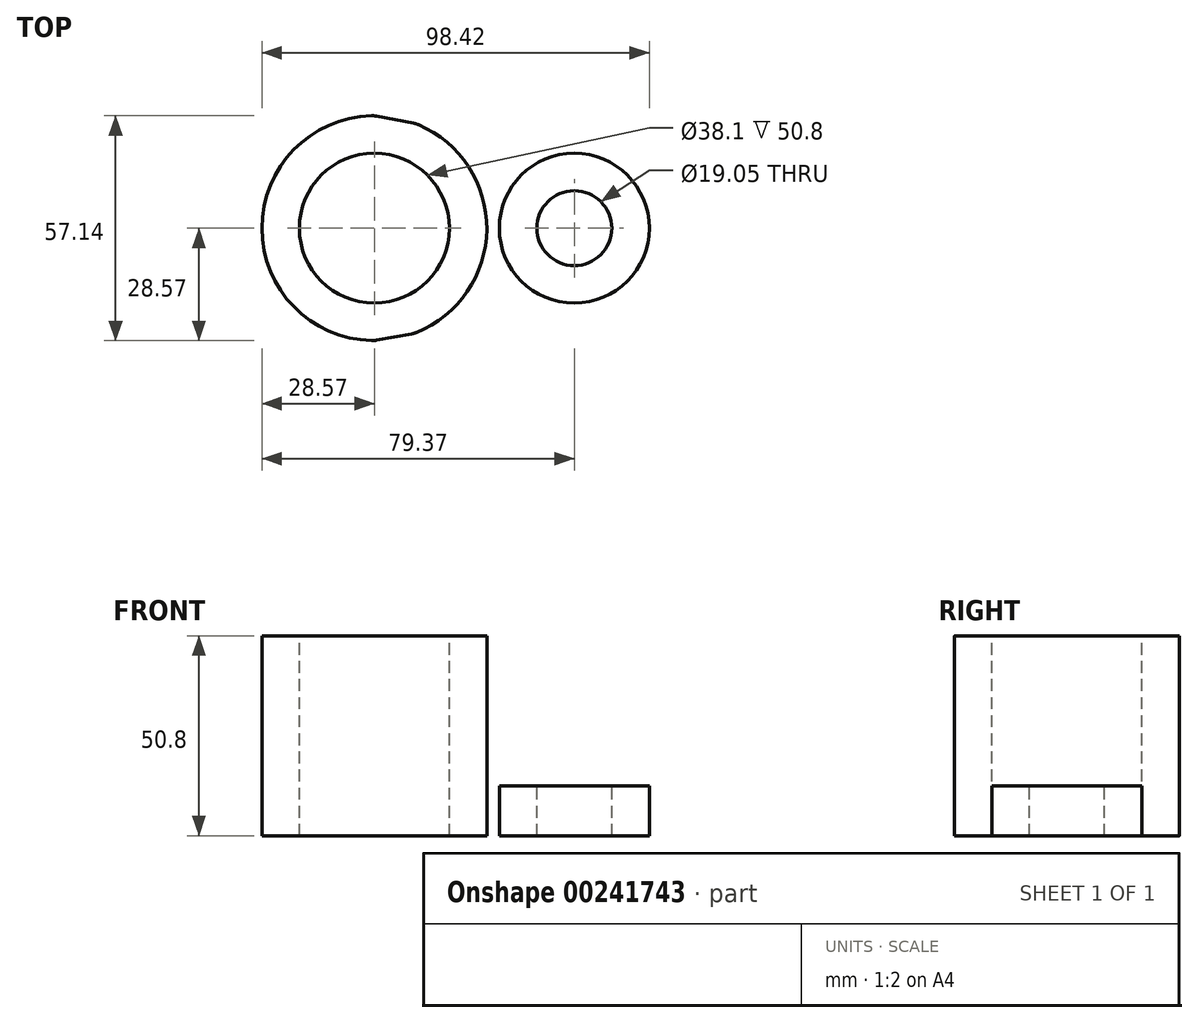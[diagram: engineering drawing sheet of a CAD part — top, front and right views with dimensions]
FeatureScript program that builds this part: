
annotation { "Feature Type Name" : "Feature", "Feature Type Description" : "" }
export const myFeature = defineFeature(function(context is Context, id is Id, definition is map)
    precondition{}
    {
        {
            var Q0;
            Q0=qCreatedBy(makeId("Top.planeOp"),FACE);
            var sketch = newSketch(context, id + "F0", { "sketchPlane" : qUnion([Q0])});
            skCircle(sketch, "E0", {"center": v(0, 0) * mm, "radius": 28.58 * mm});
            skCircle(sketch, "E1", {"center": v(0, 0) * mm, "radius": 19.05 * mm});
            skCircle(sketch, "E2", {"center": v(50.8, 0) * mm, "radius": 9.53 * mm});
            skCircle(sketch, "E3", {"center": v(50.8, 0) * mm, "radius": 19.05 * mm});
            skLineSegment(sketch, "E4", {"start": v(0, 28.57) * mm, "end": v(49.87, 19.03) * mm});
            skLineSegment(sketch, "E5", {"start": v(0, -28.58) * mm, "end": v(54.2, -18.74) * mm});
            skSolve(sketch);
        }
        {
            var Q0;
            Q0=makeQuery(id+"F0.imprint","IMPRINT",FACE,{"disambiguationData":[TD([[makeQuery(id+"F0.imprint","IMPRINT",EDGE,{"derivedFrom":sQuery(id+"F0.wireOp",EDGE,"E2")}),-1.0]])]});
            var Q1;
            {var subQ0=sQuery(id+"F0.wireOp",EDGE,"E4");var subQ1=sQuery(id+"F0.wireOp",EDGE,"E0");var subQ2=makeQuery(id+"F0.imprint","INTERSECT",VERTEX,{"disambiguationData":[OD(1.0)],"derivedFrom":[subQ1,subQ0]});Q1=makeQuery(id+"F0.imprint","IMPRINT",FACE,{"disambiguationData":[TD([[makeQuery(id+"F0.imprint","IMPRINT",EDGE,{"disambiguationData":[TD([[subQ2,1.0]])],"derivedFrom":subQ1}),-1.0]])]});}
            var Q2;
            Q2=makeQuery(id+"F0.imprint","IMPRINT",FACE,{"disambiguationData":[TD([[makeQuery(id+"F0.imprint","IMPRINT",EDGE,{"derivedFrom":sQuery(id+"F0.wireOp",EDGE,"E1")}),-1.0]])]});
            extrude(context, id + "F1", {"entities" : qUnion([Q0, Q1, Q2]), "oppositeDirection" : true, "depth" : 25.4 * mm});
        }
        {
            var Q0;
            Q0=makeQuery(id+"F0.imprint","IMPRINT",FACE,{"disambiguationData":[TD([[makeQuery(id+"F0.imprint","IMPRINT",EDGE,{"derivedFrom":sQuery(id+"F0.wireOp",EDGE,"E1")}),-1.0]])]});
            var Q1;
            {var subQ0=sQuery(id+"F0.wireOp",EDGE,"E5");var subQ1=sQuery(id+"F0.wireOp",EDGE,"E0");var subQ2=makeQuery(id+"F0.imprint","INTERSECT",VERTEX,{"disambiguationData":[OD(0.0)],"derivedFrom":[subQ1,subQ0]});Q1=makeQuery(id+"F0.imprint","IMPRINT",FACE,{"disambiguationData":[TD([[makeQuery(id+"F0.imprint","IMPRINT",EDGE,{"disambiguationData":[TD([[subQ2,-1.0]])],"derivedFrom":subQ1}),1.0]])]});}
            var Q2;
            {var subQ0=sQuery(id+"F0.wireOp",EDGE,"E4");var subQ1=sQuery(id+"F0.wireOp",EDGE,"E0");var subQ2=makeQuery(id+"F0.imprint","INTERSECT",VERTEX,{"disambiguationData":[OD(0.0)],"derivedFrom":[subQ1,subQ0]});Q2=makeQuery(id+"F0.imprint","IMPRINT",FACE,{"disambiguationData":[TD([[makeQuery(id+"F0.imprint","IMPRINT",EDGE,{"disambiguationData":[TD([[subQ2,1.0]])],"derivedFrom":subQ1}),1.0]])]});}
            extrude(context, id + "F2", {"entities" : qUnion([Q0, Q1, Q2]), "operationType" : NewBodyOperationType.ADD, "depth" : 25.4 * mm});
        }
        {
            var Q0;
            Q0=makeQuery(id+"F0.imprint","IMPRINT",FACE,{"disambiguationData":[TD([[makeQuery(id+"F0.imprint","IMPRINT",EDGE,{"derivedFrom":sQuery(id+"F0.wireOp",EDGE,"E2")}),-1.0]])]});
            extrude(context, id + "F3", {"entities" : qUnion([Q0]), "operationType" : NewBodyOperationType.REMOVE, "oppositeDirection" : true, "depth" : 12.7 * mm});
        }
        {
            var Q0;
            {var subQ0=sQuery(id+"F0.wireOp",EDGE,"E4");var subQ1=sQuery(id+"F0.wireOp",EDGE,"E3");Q0=makeQuery(id+"F3.boolean.opBoolean","SPLIT",EDGE,{"disambiguationData":[topologyDisambiguationEdgeConnected([makeQuery(id+"F3.opExtrude","SWEPT_FACE",FACE,{"disambiguationData":[OSD([subQ1])]})])],"derivedFrom":makeQuery(id+"F1.opExtrude","SWEPT_EDGE",EDGE,{"disambiguationData":[OSD([subQ1,subQ0])]})});}
            var Q1;
            {var subQ0=sQuery(id+"F0.wireOp",EDGE,"E5");var subQ1=sQuery(id+"F0.wireOp",EDGE,"E3");Q1=makeQuery(id+"F3.boolean.opBoolean","SPLIT",EDGE,{"disambiguationData":[topologyDisambiguationEdgeConnected([makeQuery(id+"F3.opExtrude","SWEPT_FACE",FACE,{"disambiguationData":[OSD([subQ1])]})])],"derivedFrom":makeQuery(id+"F1.opExtrude","SWEPT_EDGE",EDGE,{"disambiguationData":[OSD([subQ1,subQ0])]})});}
            fillet(context, id + "F4", {"entities" : qUnion([Q0, Q1]), "radius" : 6.35 * mm, "tangentPropagation" : true, "allowEdgeOverflow" : false});
        }
    });
